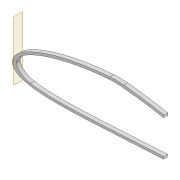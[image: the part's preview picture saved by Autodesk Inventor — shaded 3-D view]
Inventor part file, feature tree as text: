
AUTODESK INVENTOR PART (.ipt)
format: ipt  version: 2022 (Build 260153000, 153)  size: 550,400 bytes
history: native  units: mm
features: sketch x7, extrude x6, thicken_offset x4, projected_geometry x4, fillet x3, shell x1, plane x1, other x1
ambient origin geometry x8: Origin, YZ Plane, XZ Plane, XY Plane, X Axis, Y Axis, Z Axis, Center Point
bodies: Solid1 (feature_tree)
feature tree (27):
  extrude  "Extrusion1"  Depth=3.0mm
  shell  "Shell1"  Thickness=1.0mm
  thicken_offset  "Thicken1"
  extrude  "Extrusion27"  TaperAngle=0.0deg  [1 undecoded]
  thicken_offset  "Thicken3"
  extrude  "Extrusion29"  Depth=20.0mm
  plane  "Work Plane5"
  other  "Bend Part2"
  thicken_offset  "Thicken5"
  extrude  "Extrusion30"  Depth=5.0mm TaperAngle=0.0deg
  fillet  "Fillet6"  Radius=10.0mm
  extrude  "Extrusion31"  Depth=1.0mm
  fillet  "Fillet7"  Radius=50.0mm
  extrude  "Extrusion32"  Depth=5.0mm TaperAngle=0.0deg
  fillet  "Fillet8"  Radius=500.0mm
  thicken_offset  "Thicken6"
  sketch  "Sketch3"  dims[d0=5.0mm d1=0.0mm d2=3.0mm d159=1.0mm d160=2.0mm]
  sketch  "Sketch48"  dims[d236=190.0mm d237=0.0mm d238=0.0mm]
  sketch  "Sketch55"  dims[d249=2.0mm d250=1.0mm d254=20.0mm]
  projected_geometry  "Projected Loop32"
  sketch  "Sketch57"  dims[d255=8.0mm d256=5.0mm d257=0.0mm d262=10.0mm d263=0.174533mm]
  sketch  "Sketch58"  dims[d264=1.0mm d265=1.0mm d268=50.0mm]
  projected_geometry  "Projected Loop34"
  sketch  "Sketch59"  dims[d269=9.0mm d270=5.0mm d271=0.0mm d272=500.0mm]
  projected_geometry  "Projected Loop35"
  sketch  "Sketch60"  dims[d273=200.0mm d274=60.0mm d275=600.0mm d276=5.0mm d277=0.0mm d278=100.0mm d279=5.0mm d280=60.0mm d281=500.0mm d282=10.0mm d283=0.0mm d284=100.0mm d285=2.0mm d286=3.0mm]
  projected_geometry  "Projected Loop36"
note: 1 required parameter value undecoded (feature->parameter linkage not recoverable at this tier; creation-order binding heuristic only, values carry confidence <= 0.55)
